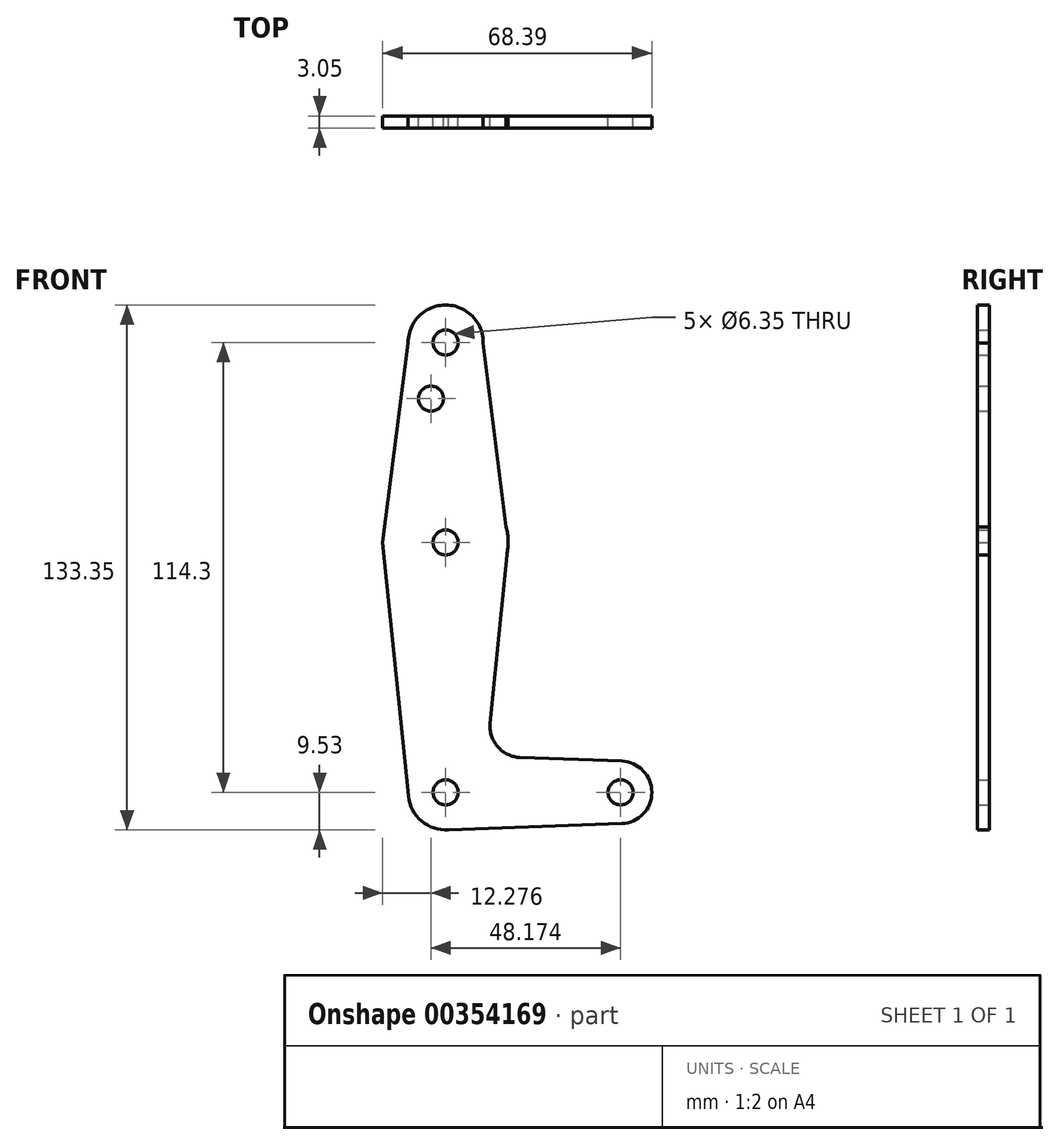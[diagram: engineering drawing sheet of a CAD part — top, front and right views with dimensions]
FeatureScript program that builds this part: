
annotation { "Feature Type Name" : "Feature", "Feature Type Description" : "" }
export const myFeature = defineFeature(function(context is Context, id is Id, definition is map)
    precondition{}
    {
        {
            var Q0;
            Q0=qCreatedBy(makeId("Front.planeOp"),FACE);
            var sketch = newSketch(context, id + "F0", { "sketchPlane" : qUnion([Q0])});
            skLineSegment(sketch, "E0", {"start": v(0, 50.8) * mm, "end": v(0, -63.5) * mm});
            skLineSegment(sketch, "E1", {"start": v(0, -63.5) * mm, "end": v(44.45, -63.5) * mm});
            skCircle(sketch, "E2", {"center": v(0, 50.8) * mm, "radius": 9.53 * mm});
            skCircle(sketch, "E3", {"center": v(0, -63.5) * mm, "radius": 9.53 * mm});
            skCircle(sketch, "E4", {"center": v(0, 0) * mm, "radius": 15.88 * mm});
            skCircle(sketch, "E5", {"center": v(44.45, -63.5) * mm, "radius": 7.94 * mm});
            skLineSegment(sketch, "E6", {"start": v(0, 0) * mm, "end": v(0, -63.5) * mm});
            skLineSegment(sketch, "E7", {"start": v(-9.52, 50.66) * mm, "end": v(-16, 0) * mm});
            skLineSegment(sketch, "E8", {"start": v(9.52, 50.67) * mm, "end": v(15.88, 0) * mm});
            skLineSegment(sketch, "E9", {"start": v(-16, 0) * mm, "end": v(-9.48, -64.46) * mm});
            skLineSegment(sketch, "E10", {"start": v(15.88, 0) * mm, "end": v(11.32, -45.92) * mm});
            skLineSegment(sketch, "E11", {"start": v(18.95, -54.65) * mm, "end": v(44.73, -55.57) * mm});
            skLineSegment(sketch, "E12", {"start": v(0, -73.03) * mm, "end": v(44.73, -71.43) * mm});
            skArc(sketch, "E13.filletArc", {"start": v(11.32, -45.92) * mm, "mid": v(13.24, -51.94) * mm, "end": v(18.95, -54.65) * mm});
            skCircle(sketch, "E14", {"center": v(0, 0) * mm, "radius": 3.18 * mm});
            skCircle(sketch, "E15", {"center": v(0, -63.5) * mm, "radius": 3.18 * mm});
            skCircle(sketch, "E16", {"center": v(44.45, -63.5) * mm, "radius": 3.18 * mm});
            skCircle(sketch, "E17", {"center": v(0, 50.8) * mm, "radius": 3.18 * mm});
            skCircle(sketch, "E18", {"center": v(-3.72, 36.53) * mm, "radius": 3.18 * mm});
            skSolve(sketch);
        }
        {
            var Q0;
            Q0 = qSketchRegion(id + "F0", true);
            var Q1;
            {var subQ0=sQuery(id+"F0.wireOp",EDGE,"E15");var subQ1=sQuery(id+"F0.wireOp",EDGE,"E1");var subQ2=makeQuery(id+"F0.imprint","INTERSECT",VERTEX,{"derivedFrom":[subQ1,subQ0]});Q1=makeQuery(id+"F0.imprint","IMPRINT",FACE,{"disambiguationData":[TD([[makeQuery(id+"F0.imprint","IMPRINT",EDGE,{"disambiguationData":[TD([[subQ2,-1.0]])],"derivedFrom":subQ1}),1.0]])]});}
            extrude(context, id + "F1", {"entities" : qUnion([Q0, Q1]), "depth" : 3.05 * mm});
        }
    });
